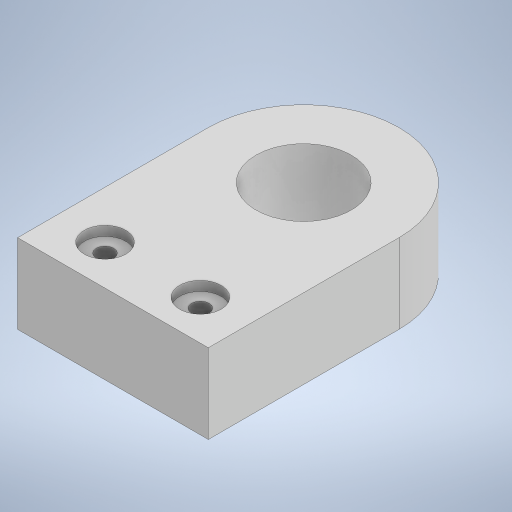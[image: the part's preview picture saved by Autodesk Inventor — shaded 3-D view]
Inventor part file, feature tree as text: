
AUTODESK INVENTOR PART (.ipt)
format: ipt  version: 2023.2 (Build 272271030, 271C)  size: 239,616 bytes
history: native  units: mm
features: extrude x3, sketch x3, projected_geometry x2
ambient origin geometry x8: Origin, YZ Plane, XZ Plane, XY Plane, X Axis, Y Axis, Z Axis, Center Point
bodies: Solid1 (feature_tree)
feature tree (8):
  extrude  "Extrusion1"  Depth=60.0mm
  extrude  "Extrusion2"  Depth=25.0mm TaperAngle=0.0deg
  extrude  "Extrusion3"  Depth=3.0mm
  sketch  "Sketch1"  dims[d0=60.0mm d1=60.0mm]
  sketch  "Sketch2"  dims[d2=30.0mm d3=25.0mm d4=0.0mm]
  projected_geometry  "Projected Loop1"
  sketch  "Sketch3"  dims[d5=65.0mm d6=5.5mm d7=30.0mm d8=0.0mm d9=0.0mm d10=13.1mm d11=13.1mm d12=3.0mm d13=0.0mm]
  projected_geometry  "Projected Loop2"
